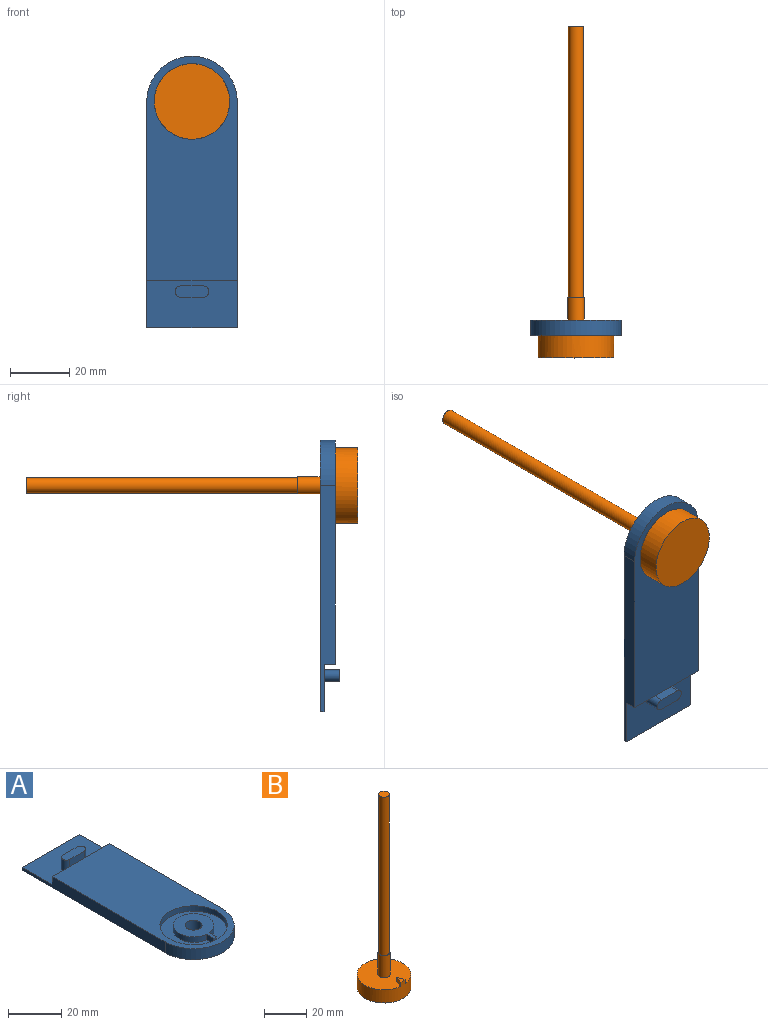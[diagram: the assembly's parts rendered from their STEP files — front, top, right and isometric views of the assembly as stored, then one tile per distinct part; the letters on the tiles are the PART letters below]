
ASSEMBLY  parts=2 mates=1
PART A: 21 faces, bbox 30.5x91.4x6.4 mm
  f0: plane 30.48x16mm, normal (0,0,1), area 447.3mm2, adj f2,f3,f4,f15,f16,f17,f18,f19
  f1: plane 75.44x30.48mm, normal (0,0,1), area 1693mm2, adj f2,f3,f5,f8,f15
  f2: plane 76.2x5.08mm, normal (1,0,0), area 326.1mm2, adj f0,f1,f4,f5,f7,f15
  f3: plane 76.2x5.08mm, normal (-1,0,0), area 326.1mm2, adj f0,f1,f4,f5,f7,f15
  f4: plane 30.48x1.27mm, normal (0,1,0), area 38.7mm2, adj f0,f2,f3,f7
  f5: cylinder r=15.24mm len=30.48mm, axis (0,0,-1), area 243.2mm2, adj f1,f2,f3,f7
  f6: plane 25.4x25.4mm, normal (0,0,1), area 319.4mm2, adj f8,f9,f10,f11,f12
  f7: plane 91.44x30.48mm, normal (0,0,-1), area 2655.7mm2, adj f2,f3,f4,f5,f14
  f8: cylinder r=12.7mm len=25.4mm, axis (0,0,-1), area 202.7mm2, adj f1,f6
  f9: cylinder r=7.62mm len=15.24mm, axis (0,0,-1), area 118.4mm2, adj f6,f10,f12,f13
  f10: plane 3.84x2.54mm, normal (-1,0,0), area 9.7mm2, adj f6,f9,f11,f13
  f11: plane 2.54x1.27mm, normal (0,-1,0), area 3.2mm2, adj f6,f10,f12,f13
  f12: plane 3.84x2.54mm, normal (1,0,0), area 9.7mm2, adj f6,f9,f11,f13
  f13: plane 19.05x15.24mm, normal (0,0,1), area 155.6mm2, adj f9,f10,f11,f12,f14
  f14: cylinder r=3.17mm len=6.35mm, axis (0,0,1), area 101.3mm2, adj f7,f13
  f15: plane 30.48x3.81mm, normal (0,1,0), area 116.1mm2, adj f0,f1,f2,f3
  f16: cylinder r=1.91mm len=5.08mm, axis (0,0,-1), area 30.4mm2, adj f0,f17,f19,f20
  f17: plane 7.62x5.08mm, normal (0,-1,0), area 38.7mm2, adj f0,f16,f18,f20
  f18: cylinder r=1.91mm len=5.08mm, axis (0,0,-1), area 30.4mm2, adj f0,f17,f19,f20
  f19: plane 7.62x5.08mm, normal (0,1,0), area 38.7mm2, adj f0,f16,f18,f20
  f20: plane 11.43x3.81mm, normal (0,0,1), area 40.4mm2, adj f16,f17,f18,f19
PART B: 10 faces, bbox 25.4x25.4x111.8 mm
  f0: plane 25.4x25.32mm, normal (0,0,1), area 474.9mm2, adj f1,f3,f4,f6
  f1: cylinder r=12.7mm len=25.4mm, axis (0,0,-1), area 615.2mm2, adj f0,f2,f3,f4,f5
  f2: plane 25.4x25.4mm, normal (0,0,-1), area 506.7mm2, adj f1
  f3: plane 4.24x2.54mm, normal (0.95,0.32,0), area 11.3mm2, adj f0,f1,f4,f5
  f4: plane 4.24x2.54mm, normal (-0.95,0.32,0), area 11.3mm2, adj f0,f1,f3,f5
  f5: plane 4.32x2.83mm, normal (0,0,1), area 6.1mm2, adj f1,f3,f4
  f6: cylinder r=2.86mm len=12.7mm, axis (0,0,-1), area 228mm2, adj f0,f7
  f7: plane 5.72x5.72mm, normal (0,0,1), area 5.4mm2, adj f6,f8
  f8: cylinder r=2.54mm len=91.44mm, axis (0,0,-1), area 1459.3mm2, adj f7,f9
  f9: plane 5.08x5.08mm, normal (0,0,1), area 20.3mm2, adj f8
PLACE A rot(axis=(0,0.71,-0.71),180deg) t=(-16.44,10.04,30.59)mm fixed
PLACE B rot(axis=(-1,0,0),90deg) t=(-16.44,-2.66,30.59)mm
MATE cylindrical B.f1 <-> A.f14  axis (0,1,0) through (-16.44,4.96,30.59)mm
